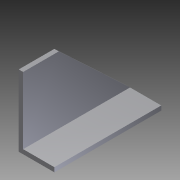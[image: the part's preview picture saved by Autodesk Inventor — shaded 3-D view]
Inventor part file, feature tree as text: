
AUTODESK INVENTOR PART (.ipt)
format: ipt  version: 2012 (Build 160160000, 160)  size: 83,968 bytes
history: native  units: in
note: dims shown in document units (in); Inventor stores cm internally (conversion verified against a paired STEP export)
features: extrude x2, sketch x2
ambient origin geometry x8: Origin, YZ Plane, XZ Plane, XY Plane, X Axis, Y Axis, Z Axis, Center Point
bodies: Solid1 (feature_tree)
feature tree (4):
  extrude  "Extrusion1"  Depth=1.0in
  extrude  "Extrusion2"  Depth=3.0in TaperAngle=0.0deg
  sketch  "Sketch1"  dims[d0=2.0in d1=1.0in]
  sketch  "Sketch2"  dims[d2=0.1242in d3=3.0in d4=0.0in d5=1.0in d6=0.125in d7=1.0in d8=0.0in]
